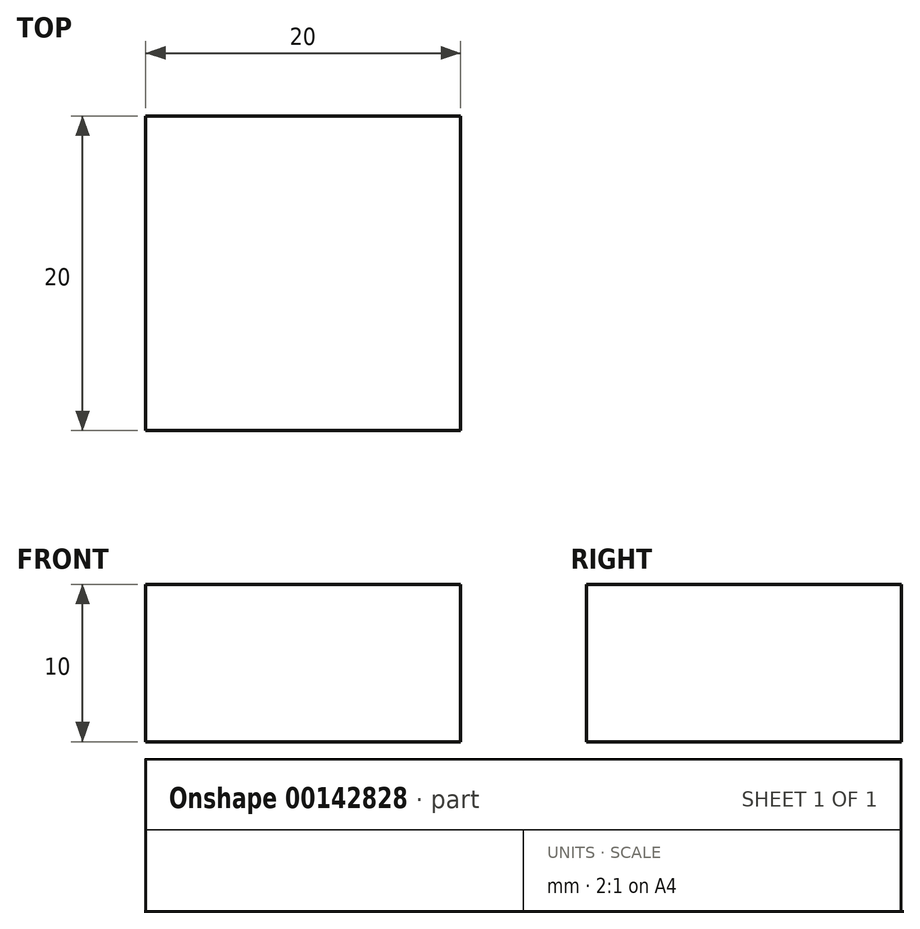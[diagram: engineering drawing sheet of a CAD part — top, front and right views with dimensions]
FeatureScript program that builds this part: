
annotation { "Feature Type Name" : "Feature", "Feature Type Description" : "" }
export const myFeature = defineFeature(function(context is Context, id is Id, definition is map)
    precondition{}
    {
        {
            var Q0;
            Q0=qCreatedBy(makeId("Top.planeOp"),FACE);
            var sketch = newSketch(context, id + "F0", { "sketchPlane" : qUnion([Q0])});
            skLineSegment(sketch, "E0.bottom", {"start": v(0, 0) * mm, "end": v(20, 0) * mm});
            skLineSegment(sketch, "E0.top", {"start": v(0, 20) * mm, "end": v(20, 20) * mm});
            skLineSegment(sketch, "E0.left", {"start": v(0, 0) * mm, "end": v(0, 20) * mm});
            skLineSegment(sketch, "E0.right", {"start": v(20, 0) * mm, "end": v(20, 20) * mm});
            skSolve(sketch);
        }
        {
            var Q0;
            Q0=makeQuery(id+"F0.imprint","IMPRINT",FACE,{"disambiguationData":[TD([[makeQuery(id+"F0.imprint","IMPRINT",EDGE,{"derivedFrom":sQuery(id+"F0.wireOp",EDGE,"E0.bottom")}),1.0]])]});
            extrude(context, id + "F1", {"entities" : qUnion([Q0]), "depth" : 10 * mm, "offsetDistance" : 25 * mm});
        }
    });
